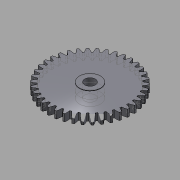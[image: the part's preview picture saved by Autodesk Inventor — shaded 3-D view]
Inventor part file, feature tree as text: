
AUTODESK INVENTOR PART (.ipt)
format: ipt  version: 2015 (Build 190159000, 159)  size: 330,752 bytes
history: native  units: in
note: dims shown in document units (in); Inventor stores cm internally (conversion verified against a paired STEP export)
features: other x13, sketch x5, plane x2
ambient origin geometry x8: Origin, YZ Plane, XZ Plane, XY Plane, X Axis, Y Axis, Z Axis, Center Point
bodies: Solid1 (feature_tree)
feature tree (20):
  other  "Spur Gear2"
  other  "Solid1::Spur Gear2"
  other  "TaggingFeature1"
  sketch  "Sketch1"  dims[d0=0.3937in]
  sketch  "Sketch2"  dims[d16=0.5709in d17=0.0in d41=0.0in d43=0.5709in d46=0.5709in d47=0.0in d48=0.0in]
  sketch  "Sketch3"
  sketch  "Sketch4"
  sketch  "Sketch5"
  plane  "XZ Plane_1"
  plane  "Work Plane2"
  other  "Z Axis_1"
  other  "Srf1"
  other  "Srf1::Derived"
  other  "Distance iMate"
  other  "Align iMate"
  other  "Mesh iMate"
  other  "Axis iMate"
  other  "Position iMate"
  other  "Mesh iMate2"
  other  "Start plane iMate"
